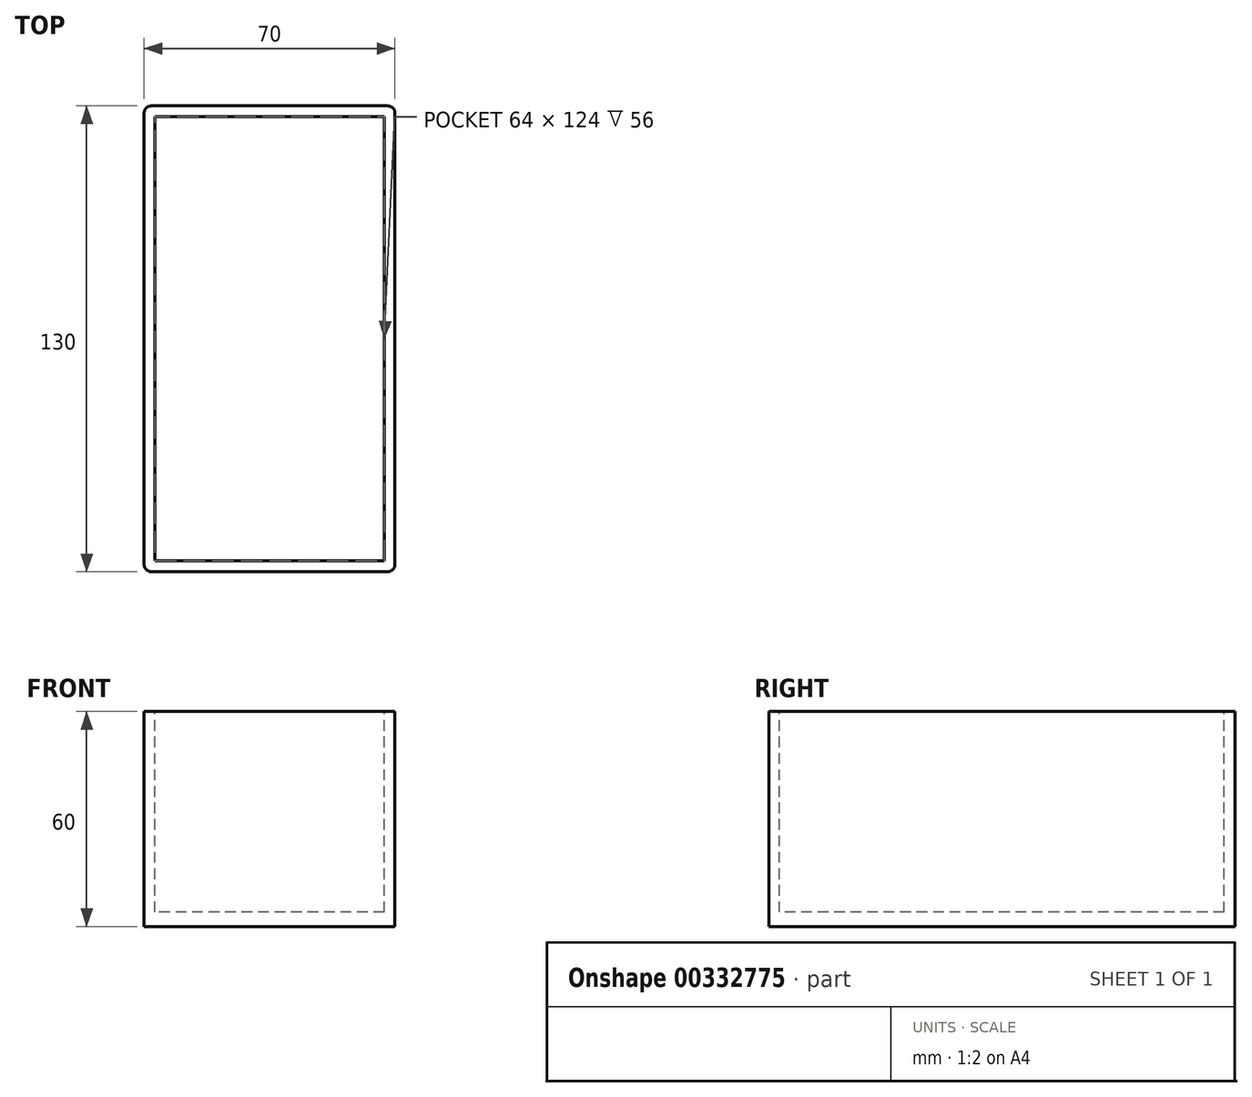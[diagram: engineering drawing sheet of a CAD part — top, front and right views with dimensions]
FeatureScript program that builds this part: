
annotation { "Feature Type Name" : "Feature", "Feature Type Description" : "" }
export const myFeature = defineFeature(function(context is Context, id is Id, definition is map)
    precondition{}
    {
        {
            var Q0;
            Q0=qCreatedBy(makeId("Top.planeOp"),FACE);
            var sketch = newSketch(context, id + "F0", { "sketchPlane" : qUnion([Q0])});
            skLineSegment(sketch, "E0.bottom", {"start": v(-36.72, 73.95) * mm, "end": v(33.28, 73.95) * mm});
            skLineSegment(sketch, "E0.top", {"start": v(-36.72, -56.05) * mm, "end": v(33.28, -56.05) * mm});
            skLineSegment(sketch, "E0.left", {"start": v(-36.72, 73.95) * mm, "end": v(-36.72, -56.05) * mm});
            skLineSegment(sketch, "E0.right", {"start": v(33.28, 73.95) * mm, "end": v(33.28, -56.05) * mm});
            skSolve(sketch);
        }
        {
            var Q0;
            Q0=makeQuery(id+"F0.imprint","IMPRINT",FACE,{"disambiguationData":[TD([[makeQuery(id+"F0.imprint","IMPRINT",EDGE,{"derivedFrom":sQuery(id+"F0.wireOp",EDGE,"E0.bottom")}),-1.0]])]});
            extrude(context, id + "F1", {"entities" : qUnion([Q0]), "depth" : 60 * mm});
        }
        {
            var Q0;
            Q0=makeQuery(id+"F1.opExtrude","SWEPT_EDGE",EDGE,{"disambiguationData":[OSD([sQuery(id+"F0.wireOp",EDGE,"E0.bottom"),sQuery(id+"F0.wireOp",EDGE,"E0.right")])]});
            var Q1;
            Q1=makeQuery(id+"F1.opExtrude","SWEPT_EDGE",EDGE,{"disambiguationData":[OSD([sQuery(id+"F0.wireOp",EDGE,"E0.top"),sQuery(id+"F0.wireOp",EDGE,"E0.right")])]});
            var Q2;
            Q2=makeQuery(id+"F1.opExtrude","SWEPT_EDGE",EDGE,{"disambiguationData":[OSD([sQuery(id+"F0.wireOp",EDGE,"E0.bottom"),sQuery(id+"F0.wireOp",EDGE,"E0.left")])]});
            var Q3;
            Q3=makeQuery(id+"F1.opExtrude","SWEPT_EDGE",EDGE,{"disambiguationData":[OSD([sQuery(id+"F0.wireOp",EDGE,"E0.top"),sQuery(id+"F0.wireOp",EDGE,"E0.left")])]});
            fillet(context, id + "F2", {"entities" : qUnion([Q0, Q1, Q2, Q3]), "radius" : 2 * mm, "tangentPropagation" : true, "allowEdgeOverflow" : false});
        }
        {
            var Q0;
            Q0=makeQuery(id+"F1.opExtrude","CAP_FACE",FACE,{"disambiguationData":[OSD([sQuery(id+"F0.wireOp",EDGE,"E0.bottom"),sQuery(id+"F0.wireOp",EDGE,"E0.top"),sQuery(id+"F0.wireOp",EDGE,"E0.left"),sQuery(id+"F0.wireOp",EDGE,"E0.right")])],"isStart":false});
            var sketch = newSketch(context, id + "F3", { "sketchPlane" : qUnion([Q0])});
            skLineSegment(sketch, "E1.0", {"start": v(-33.72, 70.95) * mm, "end": v(-33.72, -53.05) * mm});
            skLineSegment(sketch, "E1.1", {"start": v(30.28, 70.95) * mm, "end": v(-33.72, 70.95) * mm});
            skLineSegment(sketch, "E1.2", {"start": v(30.28, -53.05) * mm, "end": v(30.28, 70.95) * mm});
            skLineSegment(sketch, "E1.3", {"start": v(-33.72, -53.05) * mm, "end": v(30.28, -53.05) * mm});
            skSolve(sketch);
        }
        {
            var Q0;
            Q0=makeQuery(id+"F3.imprint","IMPRINT",FACE,{"disambiguationData":[TD([[makeQuery(id+"F3.imprint","IMPRINT",EDGE,{"derivedFrom":sQuery(id+"F3.wireOp",EDGE,"E1.0")}),1.0]])]});
            extrude(context, id + "F4", {"entities" : qUnion([Q0]), "operationType" : NewBodyOperationType.REMOVE, "oppositeDirection" : true, "depth" : 56 * mm});
        }
    });
